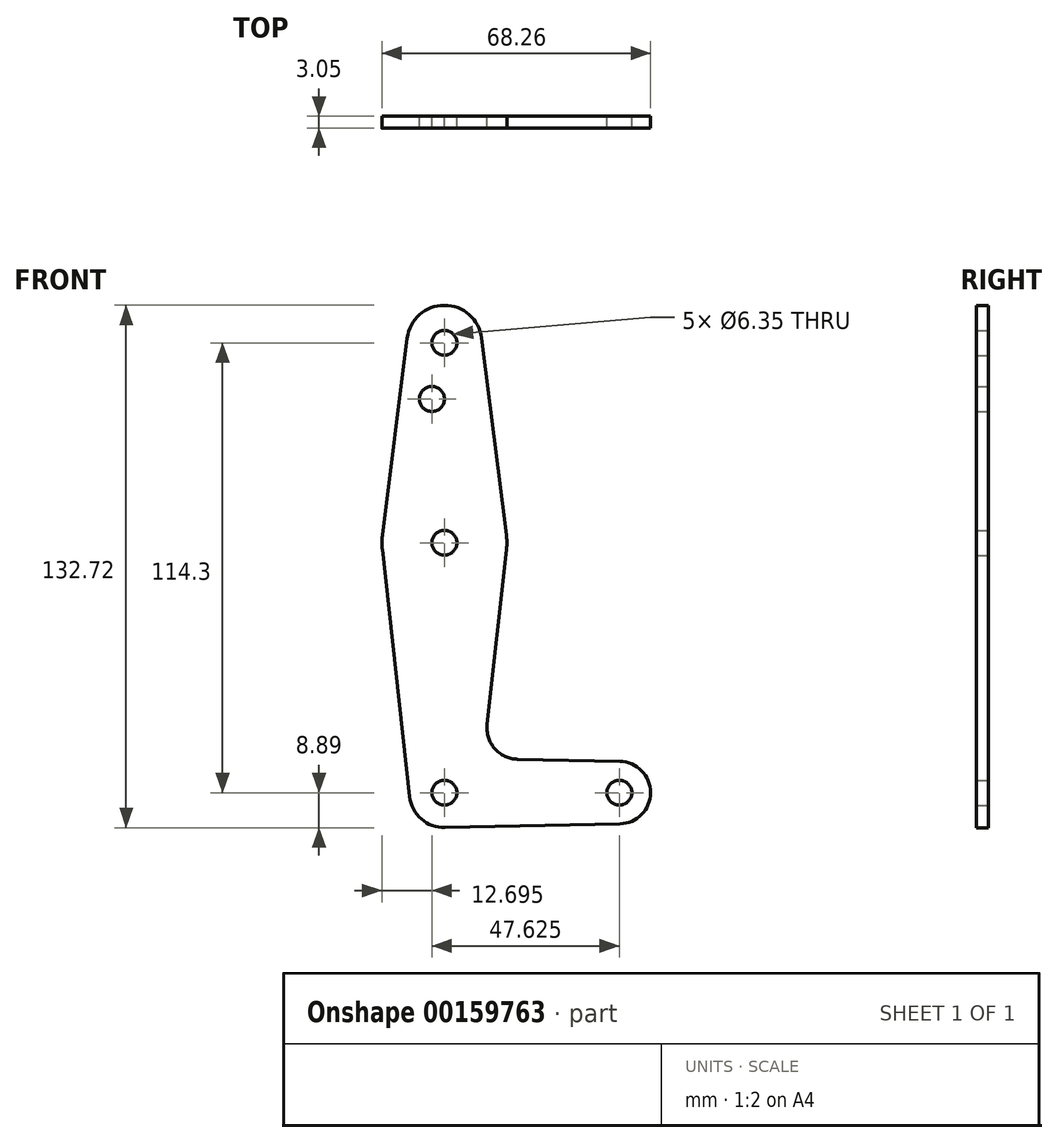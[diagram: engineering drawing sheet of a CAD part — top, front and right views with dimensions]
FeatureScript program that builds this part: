
annotation { "Feature Type Name" : "Feature", "Feature Type Description" : "" }
export const myFeature = defineFeature(function(context is Context, id is Id, definition is map)
    precondition{}
    {
        {
            var Q0;
            Q0=qCreatedBy(makeId("Front.planeOp"),FACE);
            var sketch = newSketch(context, id + "F0", { "sketchPlane" : qUnion([Q0])});
            skCircle(sketch, "E0", {"center": v(0, 0) * mm, "radius": 8.9 * mm});
            skCircle(sketch, "E1", {"center": v(0, 63.5) * mm, "radius": 15.88 * mm});
            skCircle(sketch, "E2", {"center": v(0, 114.3) * mm, "radius": 9.53 * mm});
            skCircle(sketch, "E3", {"center": v(44.45, 0) * mm, "radius": 7.94 * mm});
            skLineSegment(sketch, "E4", {"start": v(0, 0) * mm, "end": v(44.45, 0) * mm, "construction": true});
            skLineSegment(sketch, "E5", {"start": v(0, 0) * mm, "end": v(0, 63.5) * mm, "construction": true});
            skLineSegment(sketch, "E6", {"start": v(0, 63.5) * mm, "end": v(0, 114.3) * mm, "construction": true});
            skLineSegment(sketch, "E7", {"start": v(-9.45, 115.5) * mm, "end": v(-15.75, 65.48) * mm});
            skLineSegment(sketch, "E8", {"start": v(-15.78, 61.75) * mm, "end": v(-8.84, -0.98) * mm});
            skLineSegment(sketch, "E9", {"start": v(9.45, 115.5) * mm, "end": v(15.75, 65.48) * mm});
            skLineSegment(sketch, "E10", {"start": v(15.78, 61.75) * mm, "end": v(10.86, 17.32) * mm});
            skLineSegment(sketch, "E11", {"start": v(0.2, -8.89) * mm, "end": v(44.62, -7.94) * mm});
            skLineSegment(sketch, "E12", {"start": v(44.62, 7.94) * mm, "end": v(18.6, 8.5) * mm});
            skCircle(sketch, "E13", {"center": v(0, 114.3) * mm, "radius": 3.18 * mm});
            skCircle(sketch, "E14", {"center": v(0, 63.5) * mm, "radius": 3.18 * mm});
            skCircle(sketch, "E15", {"center": v(-3.18, 100.03) * mm, "radius": 3.18 * mm});
            skCircle(sketch, "E16", {"center": v(0, 0) * mm, "radius": 3.18 * mm});
            skCircle(sketch, "E17", {"center": v(44.45, 0) * mm, "radius": 3.18 * mm});
            skArc(sketch, "E18.filletArc", {"start": v(10.86, 17.32) * mm, "mid": v(12.78, 11.2) * mm, "end": v(18.6, 8.5) * mm});
            skSolve(sketch);
        }
        {
            var Q0;
            Q0 = qSketchRegion(id + "F0", true);
            extrude(context, id + "F1", {"entities" : qUnion([Q0]), "depth" : 3.05 * mm});
        }
    });
